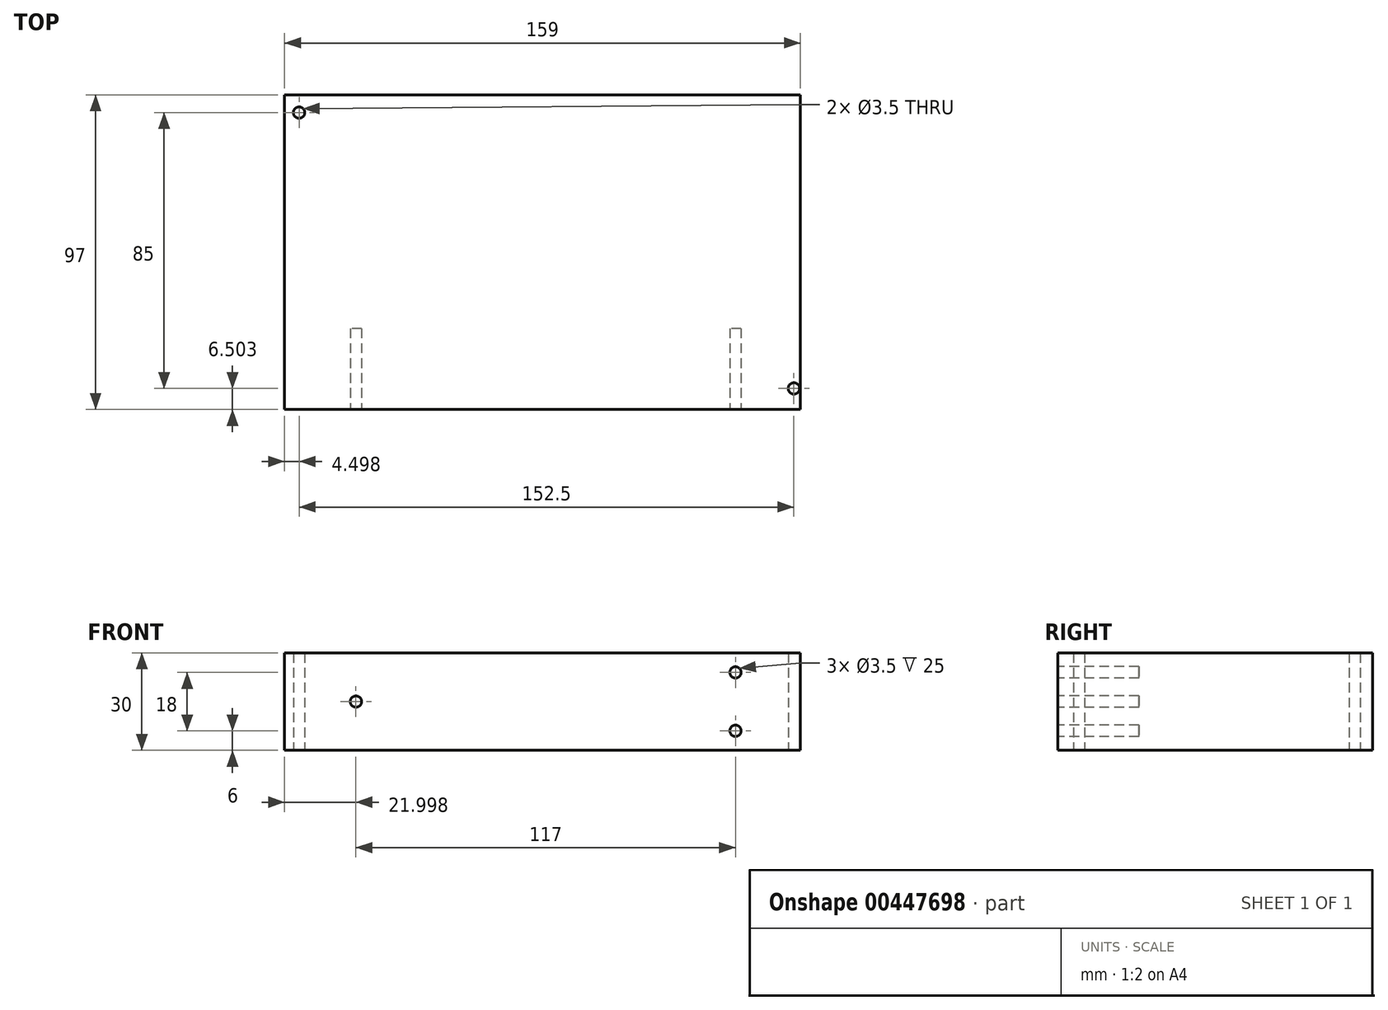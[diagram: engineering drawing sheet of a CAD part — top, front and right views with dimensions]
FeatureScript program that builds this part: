
annotation { "Feature Type Name" : "Feature", "Feature Type Description" : "" }
export const myFeature = defineFeature(function(context is Context, id is Id, definition is map)
    precondition{}
    {
        {
            var Q0;
            Q0=qCreatedBy(makeId("Top.planeOp"),FACE);
            var sketch = newSketch(context, id + "F0", { "sketchPlane" : qUnion([Q0])});
            skLineSegment(sketch, "E0.bottom", {"start": v(115.9, 18.43) * mm, "end": v(-43.1, 18.43) * mm});
            skLineSegment(sketch, "E0.top", {"start": v(115.9, 115.43) * mm, "end": v(-43.1, 115.43) * mm});
            skLineSegment(sketch, "E0.left", {"start": v(115.9, 18.43) * mm, "end": v(115.9, 115.43) * mm});
            skLineSegment(sketch, "E0.right", {"start": v(-43.1, 18.43) * mm, "end": v(-43.1, 115.43) * mm});
            skCircle(sketch, "E1", {"center": v(113.9, 24.93) * mm, "radius": 1.75 * mm});
            skCircle(sketch, "E2", {"center": v(-38.6, 109.93) * mm, "radius": 1.75 * mm});
            skSolve(sketch);
        }
        {
            var Q0;
            Q0=makeQuery(id+"F0.imprint","IMPRINT",FACE,{"disambiguationData":[TD([[makeQuery(id+"F0.imprint","IMPRINT",EDGE,{"derivedFrom":sQuery(id+"F0.wireOp",EDGE,"E0.bottom")}),-1.0]])]});
            extrude(context, id + "F1", {"entities" : qUnion([Q0]), "depth" : 30 * mm});
        }
        {
            var Q0;
            Q0=makeQuery(id+"F1.opExtrude","SWEPT_FACE",FACE,{"disambiguationData":[OSD([sQuery(id+"F0.wireOp",EDGE,"E0.bottom")])]});
            var sketch = newSketch(context, id + "F2", { "sketchPlane" : qUnion([Q0])});
            skCircle(sketch, "E3", {"center": v(-21.1, 15) * mm, "radius": 1.75 * mm});
            skCircle(sketch, "E4", {"center": v(95.9, 24) * mm, "radius": 1.75 * mm});
            skCircle(sketch, "E5", {"center": v(95.9, 6) * mm, "radius": 1.75 * mm});
            skSolve(sketch);
        }
        {
            var Q0;
            Q0 = qSketchRegion(id + "F2", true);
            extrude(context, id + "F3", {"entities" : qUnion([Q0]), "operationType" : NewBodyOperationType.REMOVE, "oppositeDirection" : true, "depth" : 25 * mm});
        }
        {
            var Q0;
            Q0=makeQuery(id+"F1.opExtrude","SWEPT_FACE",FACE,{"disambiguationData":[OSD([sQuery(id+"F0.wireOp",EDGE,"E0.bottom")])]});
            cPlane(context, id + "F4", {"entities" : qUnion([Q0]), "cplaneType" : CPlaneType.OFFSET, "offset" : 48.5 * mm, "oppositeDirection" : true, "width" : 150 * mm, "height" : 150 * mm});
        }
    });
